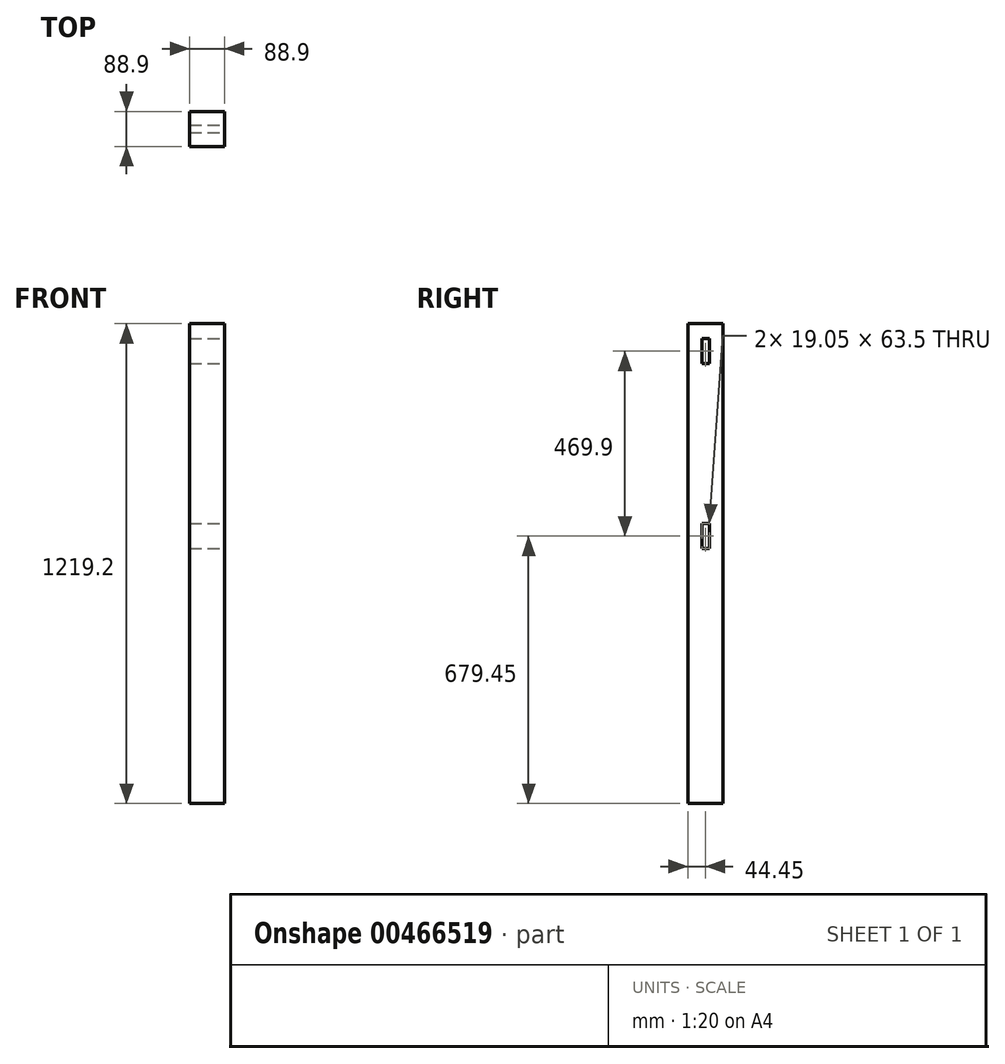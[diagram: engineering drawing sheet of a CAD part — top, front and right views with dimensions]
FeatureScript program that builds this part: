
annotation { "Feature Type Name" : "Feature", "Feature Type Description" : "" }
export const myFeature = defineFeature(function(context is Context, id is Id, definition is map)
    precondition{}
    {
        {
            var Q0;
            Q0=qCreatedBy(makeId("Top.planeOp"),FACE);
            var sketch = newSketch(context, id + "F0", { "sketchPlane" : qUnion([Q0])});
            skLineSegment(sketch, "E0.bottom", {"start": v(44.45, -44.45) * mm, "end": v(-44.45, -44.45) * mm});
            skLineSegment(sketch, "E0.top", {"start": v(44.45, 44.45) * mm, "end": v(-44.45, 44.45) * mm});
            skLineSegment(sketch, "E0.left", {"start": v(44.45, -44.45) * mm, "end": v(44.45, 44.45) * mm});
            skLineSegment(sketch, "E0.right", {"start": v(-44.45, -44.45) * mm, "end": v(-44.45, 44.45) * mm});
            skPoint(sketch, "E0.middle", {"position": v(0, 0) * mm});
            skSolve(sketch);
        }
        {
            var Q0;
            Q0=makeQuery(id+"F0.imprint","IMPRINT",FACE,{"disambiguationData":[TD([[makeQuery(id+"F0.imprint","IMPRINT",EDGE,{"derivedFrom":sQuery(id+"F0.wireOp",EDGE,"E0.bottom")}),-1.0]])]});
            extrude(context, id + "F1", {"entities" : qUnion([Q0]), "depth" : 1219.2 * mm});
        }
        {
            var Q0;
            Q0=makeQuery(id+"F1.opExtrude","SWEPT_FACE",FACE,{"disambiguationData":[OSD([sQuery(id+"F0.wireOp",EDGE,"E0.left")])]});
            var sketch = newSketch(context, id + "F2", { "sketchPlane" : qUnion([Q0])});
            skLineSegment(sketch, "E1.bottom", {"start": v(9.52, 647.7) * mm, "end": v(-9.53, 647.7) * mm});
            skLineSegment(sketch, "E1.top", {"start": v(9.52, 711.2) * mm, "end": v(-9.53, 711.2) * mm});
            skLineSegment(sketch, "E1.left", {"start": v(9.52, 647.7) * mm, "end": v(9.52, 711.2) * mm});
            skLineSegment(sketch, "E1.right", {"start": v(-9.53, 647.7) * mm, "end": v(-9.53, 711.2) * mm});
            skPoint(sketch, "E1.middle", {"position": v(0, 679.45) * mm});
            skLineSegment(sketch, "E2.bottom", {"start": v(-9.52, 1181.1) * mm, "end": v(9.53, 1181.1) * mm});
            skLineSegment(sketch, "E2.top", {"start": v(-9.52, 1117.6) * mm, "end": v(9.53, 1117.6) * mm});
            skLineSegment(sketch, "E2.left", {"start": v(-9.52, 1181.1) * mm, "end": v(-9.52, 1117.6) * mm});
            skLineSegment(sketch, "E2.right", {"start": v(9.53, 1181.1) * mm, "end": v(9.53, 1117.6) * mm});
            skPoint(sketch, "E2.middle", {"position": v(0, 1149.35) * mm});
            skSolve(sketch);
        }
        {
            var Q0;
            Q0 = qSketchRegion(id + "F2", true);
            extrude(context, id + "F3", {"entities" : qUnion([Q0]), "operationType" : NewBodyOperationType.REMOVE, "endBound" : BoundingType.THROUGH_ALL, "oppositeDirection" : true, "depth" : 25.4 * mm});
        }
    });
